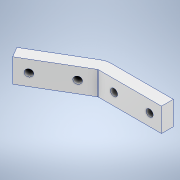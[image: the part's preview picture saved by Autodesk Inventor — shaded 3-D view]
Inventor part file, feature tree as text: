
AUTODESK INVENTOR PART (.ipt)
format: ipt  version: 2020.2 (Build 242310000, 310)  size: 201,728 bytes
history: native  units: mm
features: other x4, sketch x3, extrude x2, hole x2
ambient origin geometry x8: Origin, YZ Plane, XZ Plane, XY Plane, X Axis, Y Axis, Z Axis, Center Point
bodies: Body1 (feature_tree)
feature tree (11):
  other  "ソリッド1"
  sketch  "スケッチ1"
  extrude  "押し出し1"  Depth=10.0mm
  hole  "穴1"  [1 undecoded]
  sketch  "スケッチ2"
  extrude  "押し出し2"  Depth=5.0mm TaperAngle=0.0deg
  hole  "穴2"  [1 undecoded]
  other  "曲げパーツ1"
  sketch  "スケッチ3"
  other  "断面エッジを投影1"
  other  "断面エッジを投影2"
note: 2 required parameter values undecoded (feature->parameter linkage not recoverable at this tier; creation-order binding heuristic only, values carry confidence <= 0.55)
